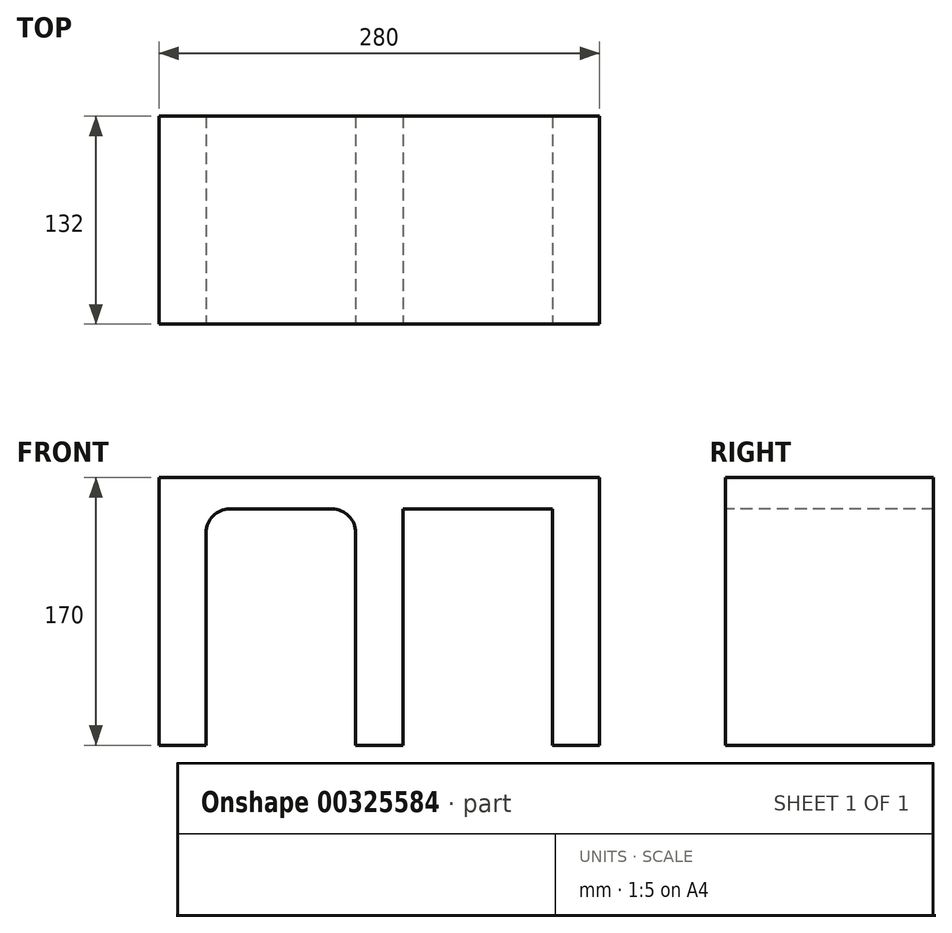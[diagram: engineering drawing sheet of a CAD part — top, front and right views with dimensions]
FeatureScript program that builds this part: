
annotation { "Feature Type Name" : "Feature", "Feature Type Description" : "" }
export const myFeature = defineFeature(function(context is Context, id is Id, definition is map)
    precondition{}
    {
        {
            var Q0;
            Q0=qCreatedBy(makeId("Top.planeOp"),FACE);
            var sketch = newSketch(context, id + "F0", { "sketchPlane" : qUnion([Q0])});
            skLineSegment(sketch, "E0.bottom", {"start": v(-143.18, 32.06) * mm, "end": v(136.82, 32.06) * mm});
            skLineSegment(sketch, "E0.top", {"start": v(-143.18, -99.94) * mm, "end": v(136.82, -99.94) * mm});
            skLineSegment(sketch, "E0.left", {"start": v(-143.18, 32.06) * mm, "end": v(-143.18, -99.94) * mm});
            skLineSegment(sketch, "E0.right", {"start": v(136.82, 32.06) * mm, "end": v(136.82, -99.94) * mm});
            skSolve(sketch);
        }
        {
            var Q0;
            Q0 = qSketchRegion(id + "F0", true);
            extrude(context, id + "F1", {"entities" : qUnion([Q0]), "depth" : 20 * mm});
        }
        {
            var Q0;
            Q0=makeQuery(id+"F1.opExtrude","CAP_FACE",FACE,{"disambiguationData":[OSD([sQuery(id+"F0.wireOp",EDGE,"E0.bottom"),sQuery(id+"F0.wireOp",EDGE,"E0.top"),sQuery(id+"F0.wireOp",EDGE,"E0.left"),sQuery(id+"F0.wireOp",EDGE,"E0.right")])],"isStart":true});
            var sketch = newSketch(context, id + "F2", { "sketchPlane" : qUnion([Q0])});
            skLineSegment(sketch, "E1.bottom", {"start": v(136.82, -32.06) * mm, "end": v(106.82, -32.06) * mm});
            skLineSegment(sketch, "E1.top", {"start": v(136.82, 99.94) * mm, "end": v(106.82, 99.94) * mm});
            skLineSegment(sketch, "E1.left", {"start": v(136.82, -32.06) * mm, "end": v(136.82, 99.94) * mm});
            skLineSegment(sketch, "E1.right", {"start": v(106.82, -32.06) * mm, "end": v(106.82, 99.94) * mm});
            skLineSegment(sketch, "E2.bottom", {"start": v(11.82, -32.06) * mm, "end": v(-18.18, -32.06) * mm});
            skLineSegment(sketch, "E2.top", {"start": v(11.82, 99.94) * mm, "end": v(-18.18, 99.94) * mm});
            skLineSegment(sketch, "E2.left", {"start": v(11.82, -32.06) * mm, "end": v(11.82, 99.94) * mm});
            skLineSegment(sketch, "E2.right", {"start": v(-18.18, -32.06) * mm, "end": v(-18.18, 99.94) * mm});
            skLineSegment(sketch, "E3.bottom", {"start": v(-113.18, -32.06) * mm, "end": v(-143.18, -32.06) * mm});
            skLineSegment(sketch, "E3.top", {"start": v(-113.18, 99.94) * mm, "end": v(-143.18, 99.94) * mm});
            skLineSegment(sketch, "E3.left", {"start": v(-113.18, -32.06) * mm, "end": v(-113.18, 99.94) * mm});
            skLineSegment(sketch, "E3.right", {"start": v(-143.18, -32.06) * mm, "end": v(-143.18, 99.94) * mm});
            skSolve(sketch);
        }
        {
            var Q0;
            Q0=makeQuery(id+"F2.imprint","IMPRINT",FACE,{"disambiguationData":[TD([[makeQuery(id+"F2.imprint","IMPRINT",EDGE,{"derivedFrom":sQuery(id+"F2.wireOp",EDGE,"E1.bottom")}),1.0]])]});
            var Q1;
            Q1=makeQuery(id+"F2.imprint","IMPRINT",FACE,{"disambiguationData":[TD([[makeQuery(id+"F2.imprint","IMPRINT",EDGE,{"derivedFrom":sQuery(id+"F2.wireOp",EDGE,"E2.bottom")}),1.0]])]});
            var Q2;
            Q2=makeQuery(id+"F2.imprint","IMPRINT",FACE,{"disambiguationData":[TD([[makeQuery(id+"F2.imprint","IMPRINT",EDGE,{"derivedFrom":sQuery(id+"F2.wireOp",EDGE,"E3.bottom")}),1.0]])]});
            extrude(context, id + "F3", {"entities" : qUnion([Q0, Q1, Q2]), "operationType" : NewBodyOperationType.ADD, "depth" : 150 * mm});
        }
        {
            var Q0;
            Q0=makeQuery(id+"F3.opExtrude","CAP_EDGE",EDGE,{"disambiguationData":[OSD([sQuery(id+"F2.wireOp",EDGE,"E1.right")])],"isStart":true});
            var Q1;
            Q1=makeQuery(id+"F3.opExtrude","CAP_EDGE",EDGE,{"disambiguationData":[OSD([sQuery(id+"F2.wireOp",EDGE,"E2.right")])],"isStart":true});
            fillet(context, id + "F4", {"entities" : qUnion([Q0, Q1]), "radius" : 15 * mm, "tangentPropagation" : true, "allowEdgeOverflow" : false});
        }
        {
            var Q0;
            Q0=makeQuery(id+"F3.opExtrude","CAP_EDGE",EDGE,{"disambiguationData":[OSD([sQuery(id+"F2.wireOp",EDGE,"E3.left")])],"isStart":true});
            var Q1;
            Q1=makeQuery(id+"F3.opExtrude","CAP_EDGE",EDGE,{"disambiguationData":[OSD([sQuery(id+"F2.wireOp",EDGE,"E2.left")])],"isStart":true});
            fillet(context, id + "F5", {"entities" : qUnion([Q0, Q1]), "radius" : 15 * mm, "tangentPropagation" : true, "allowEdgeOverflow" : false});
        }
    });
